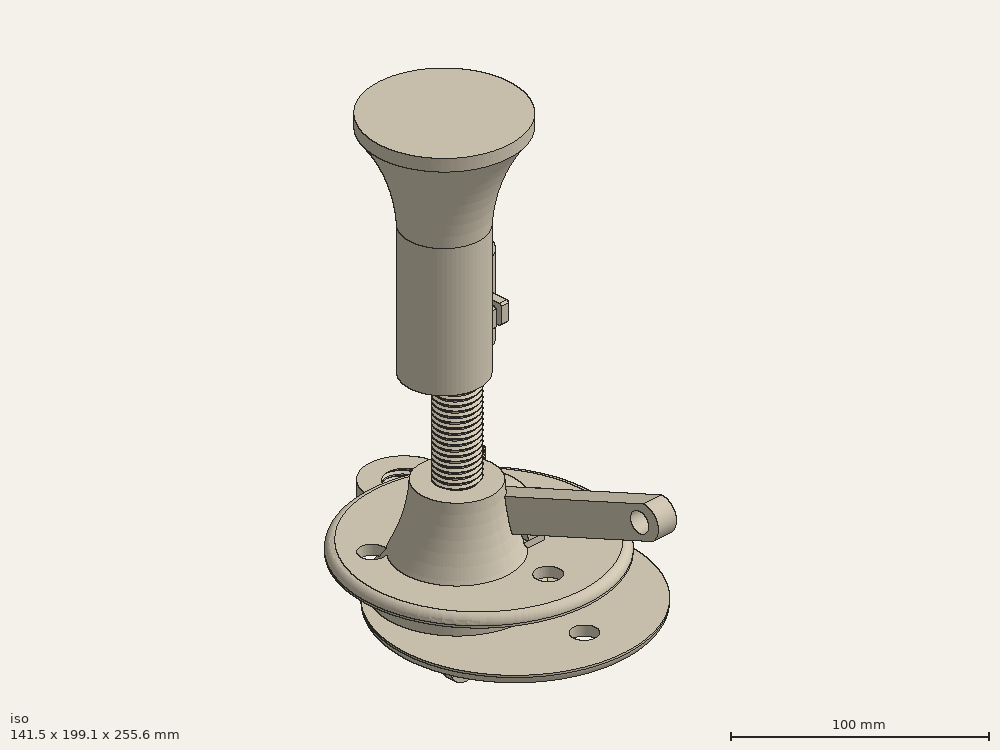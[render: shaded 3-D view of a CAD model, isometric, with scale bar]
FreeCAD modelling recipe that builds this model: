
FCSTD DOCUMENT  (FreeCAD 0.17R13541 (Git))
Label: Projector_stand
License: All rights reserved
LicenseURL: http://en.wikipedia.org/wiki/All_rights_reserved
objects: Sketcher::SketchObject×14, PartDesign::Body×8, Part::Feature×8, PartDesign::Pad×7, Part::Cut×7, Part::MultiFuse×4, Part::Box×4, Part::Cylinder×3, App::Part×3, PartDesign::Pocket×3, PartDesign::Groove×2, Part::Chamfer×2, PartDesign::Fillet×2, PartDesign::FeatureBase×2, Part::Extrusion×1
note: 79 computed .brp shape members not serialized (recipe doc carries the construction recipe); baked Part::Feature solids carry a one-line shape summary decoded from their .brp

FEATURE [Sketcher::SketchObject] Sketch
  MapMode = 5
  Support = -> [XY_Plane001]
  sketch-geometry (1):
    g0: Circle CenterX=0 CenterY=0 CenterZ=0 NormalX=0 NormalY=0 NormalZ=1 AngleXU=0 Radius=35.1414
  constraints (1):
    c: Coincident(g0,g-1)
FEATURE [PartDesign::Pad] Pad
  Length = 50
  Length2 = 100
  Profile = -> Sketch
  Type = 0
FEATURE [Sketcher::SketchObject] Sketch001
  MapMode = 5
  Placement = pos=(0,0,0) rot=(0.57735,0.57735,0.57735;2.0944rad)
  Support = -> [YZ_Plane001]
  sketch-geometry (1):
    g0: Circle CenterX=-96.2321 CenterY=54.218 CenterZ=0 NormalX=0 NormalY=0 NormalZ=1 AngleXU=0 Radius=77.7621
FEATURE [PartDesign::Groove] Groove
  Angle = 360
  Axis = (0,0,1)
  Base = (0,0,0)
  BaseFeature = -> Pad
  Profile = -> Sketch001
  ReferenceAxis = -> Z_Axis001
  Reversed = true
FEATURE [PartDesign::Body] Body
  Group = -> [Sketch,Pad,Sketch001,Groove]
  Origin = -> Origin001
  Tip = -> Groove
FEATURE [Part::Feature] Part__Feature  label="ScrewTap-M20x100_"
  Placement = pos=(0,0,149.5) rot=(0,0,1;0rad)
  shape: bbox 26.45 x 29.66 x 107.5 mm, 170 faces (baked)
FEATURE [Sketcher::SketchObject] Sketch002
  MapMode = 5
  Support = -> [XY_Plane002]
  sketch-geometry (1):
    g0: Circle CenterX=0 CenterY=0 CenterZ=0 NormalX=0 NormalY=0 NormalZ=1 AngleXU=0 Radius=35.1414
  constraints (1):
    c: Coincident(g0,g-1)
FEATURE [PartDesign::Pad] Pad001
  Length = 50
  Length2 = 100
  Profile = -> Sketch002
  Type = 0
FEATURE [Sketcher::SketchObject] Sketch003
  MapMode = 5
  Placement = pos=(0,0,0) rot=(0.57735,0.57735,0.57735;2.0944rad)
  Support = -> [YZ_Plane002]
  sketch-geometry (1):
    g0: Circle CenterX=-96.2321 CenterY=54.218 CenterZ=0 NormalX=0 NormalY=0 NormalZ=1 AngleXU=0 Radius=77.7621
FEATURE [PartDesign::Groove] Groove001
  Angle = 360
  Axis = (0,0,1)
  Base = (0,0,0)
  BaseFeature = -> Pad001
  Profile = -> Sketch003
  ReferenceAxis = -> Z_Axis002
  Reversed = true
FEATURE [PartDesign::Body] Body001
  Group = -> [Sketch002,Pad001,Sketch003,Groove001]
  Origin = -> Origin002
  Placement = pos=(75,0,0) rot=(0,0,1;0rad)
  Tip = -> Groove001
FEATURE [Part::MultiFuse] Fusion  label="Press_fit_bottom"
  Shapes = -> [Body,Part__Feature]
FEATURE [Part::Feature] Part__Feature001  label="ScrewTap-M20x100_001"
  Placement = pos=(75,0,116.5) rot=(0,0,1;0rad)
  shape: bbox 26.45 x 29.66 x 107.5 mm, 170 faces (baked)
FEATURE [Part::Cylinder] Cylinder
  Angle = 360
  AttacherType = Attacher::AttachEngine3D
  Height = 66
  Placement = pos=(75,0,50) rot=(0,0,1;0rad)
  Radius = 18.6
FEATURE [Part::MultiFuse] Fusion001
  Shapes = -> [Cylinder,Body001]
FEATURE [Part::Cut] Cut  label="Press_fit_top"
  Base = -> Fusion001
  Placement = pos=(-82,0,217) rot=(1,0,0;3.14159rad)
  Tool = -> Part__Feature001
FEATURE [Part::Cylinder] Cylinder001
  Angle = 360
  AttacherType = Attacher::AttachEngine3D
  Height = 10
  Placement = pos=(75,80,50) rot=(0,0,1;0rad)
  Radius = 18.5
FEATURE [Part::Feature] Part__Feature002  label="ScrewTap-M20x100_002"
  Placement = pos=(75,80,130.5) rot=(0,0,1;0rad)
  shape: bbox 26.45 x 29.66 x 107.5 mm, 170 faces (baked)
FEATURE [Part::Cut] Cut001
  Base = -> Cylinder001
  Tool = -> Part__Feature002
FEATURE [Part::Feature] Part__Feature003  label="Lock_screw"
  Placement = pos=(66,53,0) rot=(0,1,0;3.14159rad)
  shape: bbox 7.201 x 7 x 20.61 mm, 115 faces (baked)
FEATURE [Part::Box] Box  label="Cube"
  AttacherType = Attacher::AttachEngine3D
  Height = 10
  Length = 13
  Placement = pos=(68.5,52,50) rot=(0,0,1;0rad)
  Width = 14
FEATURE [Part::Feature] Part__Feature004  label="ISO14579-M4x16_001"
  Placement = pos=(82,57,55) rot=(0,1,0;1.5708rad)
  shape: bbox 20.61 x 7 x 7.201 mm, 115 faces (baked)
FEATURE [Part::Box] Box001  label="Cube001"
  AttacherType = Attacher::AttachEngine3D
  Height = 10
  Length = 3
  Placement = pos=(73.5,51,50) rot=(0,0,1;0rad)
  Width = 22
FEATURE [Part::MultiFuse] Fusion002
  Shapes = -> [Box,Cut001]
FEATURE [Part::Cut] Cut002
  Base = -> Fusion002
  Tool = -> Box001
FEATURE [Part::Cut] Cut003
  Base = -> Cut002
  Tool = -> Part__Feature004
FEATURE [Part::Chamfer] Chamfer  label="Lock"
  Base = -> Cut003
  Edges = 9 edges r=1: [Edge1,Edge2,Edge4,Edge12,Edge167,Edge168,Edge169,Edge199,Edge200]
  Placement = pos=(-37,-13,-53) rot=(0,0,1;0rad)
FEATURE [App::Part] Part  label="Projector holder"
  Group = -> [Body,Part__Feature,Fusion,Fusion001,Part__Feature001,Body001,Cylinder,Cut,Part__Feature003,Cut002,Cut003,Fusion002,Cut001,Part__Feature002,Cylinder001,Box,Box001,Part__Feature004,Chamfer]
  License = CC BY 3.0
  LicenseURL = http://creativecommons.org/licenses/by/3.0/
  Origin = -> Origin
  Placement = pos=(0,-127,0) rot=(0,0,1;0rad)
FEATURE [Part::Feature] Part__Feature005  label="ISO14579-M4x16_002"
  Placement = pos=(82,57,71) rot=(0,1,0;1.5708rad)
  shape: bbox 20.61 x 7 x 7.201 mm, 115 faces (baked)
FEATURE [Part::Feature] Part__Feature006  label="Shaft_Lock_Screw"
  Placement = pos=(66,53,0) rot=(0,1,0;3.14159rad)
  shape: bbox 7.201 x 7 x 20.61 mm, 115 faces (baked)
FEATURE [Part::Feature] Part__Feature007  label="ScrewTap-M20x100_003"
  Placement = pos=(75,80,130.5) rot=(0,0,1;0rad)
  shape: bbox 26.45 x 29.66 x 107.5 mm, 170 faces (baked)
FEATURE [Part::Cylinder] Cylinder002
  Angle = 360
  AttacherType = Attacher::AttachEngine3D
  Height = 40
  Placement = pos=(75,80,50) rot=(0,0,1;0rad)
  Radius = 18.5
FEATURE [Part::Cut] Cut006
  Base = -> Cylinder002
  Tool = -> Part__Feature007
FEATURE [Part::Box] Box002  label="Cube002"
  AttacherType = Attacher::AttachEngine3D
  Height = 10
  Length = 13
  Placement = pos=(68.5,52,66) rot=(0,0,1;0rad)
  Width = 14
FEATURE [Part::MultiFuse] Fusion003
  Shapes = -> [Box002,Cut006]
FEATURE [Part::Box] Box003  label="Cube003"
  AttacherType = Attacher::AttachEngine3D
  Height = 42
  Length = 3
  Placement = pos=(73.5,51,50) rot=(0,0,1;0rad)
  Width = 22
FEATURE [Part::Cut] Cut005
  Base = -> Fusion003
  Tool = -> Box003
FEATURE [Part::Cut] Cut004
  Base = -> Cut005
  Tool = -> Part__Feature005
FEATURE [Part::Chamfer] Chamfer001
  Base = -> Cut004
  Edges = 10 edges r=1: [Edge1,Edge2,Edge4,Edge12,Edge13,Edge351,Edge352,Edge353,Edge354,Edge356]
FEATURE [Sketcher::SketchObject] Sketch006
  MapMode = 5
  Placement = pos=(0,0,0) rot=(0.57735,0.57735,0.57735;2.0944rad)
  Support = -> [YZ_Plane005]
  sketch-geometry (4):
    g0: LineSegment StartX=-5.65339 StartY=-7.82598 StartZ=0 EndX=100 EndY=-7.82598 EndZ=0
    g1: LineSegment StartX=100 StartY=7.82598 StartZ=0 EndX=-5.65339 EndY=7.82598 EndZ=0
    g2: ArcOfCircle CenterX=-2.71339 CenterY=0 CenterZ=0 NormalX=0 NormalY=0 NormalZ=1 AngleXU=0 Radius=8.36 StartAngle=1.93016 EndAngle=4.35303
    g3: ArcOfCircle CenterX=97.06 CenterY=0 CenterZ=0 NormalX=0 NormalY=0 NormalZ=1 AngleXU=0 Radius=8.36 StartAngle=5.07175 EndAngle=7.49462
  constraints (12):
    c: Horizontal(g0)
    c: Horizontal(g1)
    c: Equal(g1,g0)
    c: PointOnObject(g2,g-1)
    c: Coincident(g2,g1)
    c: Coincident(g2,g0)
    c: PointOnObject(g3,g-1)
    c: Coincident(g3,g1)
    c: Coincident(g3,g0)
    c: Radius(g2) = 8.36
    c: Equal(g0,g1)
    c: DistanceX(g-1,g0) = 100
FEATURE [PartDesign::Pad] Pad002
  Length = 10
  Length2 = 100
  Placement = pos=(0,0,0) rot=(0.57735,0.57735,0.57735;2.0944rad)
  Profile = -> Sketch006
  Type = 0
FEATURE [Sketcher::SketchObject] Sketch007
  MapMode = 5
  Placement = pos=(0,0,0) rot=(0.57735,0.57735,0.57735;2.0944rad)
  Support = -> [YZ_Plane005]
  sketch-geometry (2):
    g0: Circle CenterX=-1 CenterY=0 CenterZ=0 NormalX=0 NormalY=0 NormalZ=1 AngleXU=0 Radius=5
    g1: Circle CenterX=95 CenterY=0.096219 CenterZ=0 NormalX=0 NormalY=0 NormalZ=1 AngleXU=0 Radius=5
  constraints (5):
    c: PointOnObject(g0,g-1)
    c: DistanceX(g0,g1) = 96
    c: DistanceX(g0,g-1) = 1
    c: Radius(g0) = 5
    c: Radius(g1) = 5
FEATURE [PartDesign::Pocket] Pocket001
  BaseFeature = -> Pad002
  Length = 11
  Length2 = 100
  Placement = pos=(0,0,0) rot=(0.57735,0.57735,0.57735;2.0944rad)
  Profile = -> Sketch007
  Reversed = true
  Type = 0
FEATURE [PartDesign::Body] Body003  label="Arm_shaft"
  Group = -> [Sketch006,Pad002,Sketch007,Pocket001]
  Origin = -> Origin005
  Placement = pos=(10,-1,31) rot=(1,0,0;2.79253rad)
  Tip = -> Pocket001
FEATURE [Sketcher::SketchObject] Sketch008
  MapMode = 5
  Placement = pos=(0,0,0) rot=(0.57735,0.57735,0.57735;2.0944rad)
  Support = -> [YZ_Plane007]
  sketch-geometry (5):
    g0: ArcOfCircle CenterX=0 CenterY=0 CenterZ=0 NormalX=0 NormalY=0 NormalZ=1 AngleXU=0 Radius=18.0424 StartAngle=4.71239 EndAngle=7.85398
    g1: LineSegment StartX=0 StartY=-18.0424 StartZ=0 EndX=-5.9579 EndY=-18.0424 EndZ=0
    g2: LineSegment StartX=-5.9579 StartY=-18.0424 StartZ=0 EndX=-5.9579 EndY=18.0424 EndZ=0
    g3: LineSegment StartX=0 StartY=18.0424 StartZ=0 EndX=-5.9579 EndY=18.0424 EndZ=0
    g4: Circle CenterX=10 CenterY=0 CenterZ=0 NormalX=0 NormalY=0 NormalZ=1 AngleXU=0 Radius=5
  constraints (13):
    c: Coincident(g0,g-1)
    c: PointOnObject(g0,g-2)
    c: PointOnObject(g0,g-2)
    c: Coincident(g1,g0)
    c: Horizontal(g1)
    c: Coincident(g2,g1)
    c: Vertical(g2)
    c: Coincident(g3,g0)
    c: Coincident(g3,g2)
    c: Horizontal(g3)
    c: PointOnObject(g4,g-1)
    c: Radius(g4) = 5
    c: DistanceX(g-1,g4) = 10
FEATURE [PartDesign::Pad] Pad003
  Length = 30
  Length2 = 100
  Placement = pos=(0,0,0) rot=(0.57735,0.57735,0.57735;2.0944rad)
  Profile = -> Sketch008
  Type = 0
FEATURE [Sketcher::SketchObject] Sketch009
  MapMode = 5
  Support = -> [XY_Plane007]
  sketch-geometry (4):
    g0: LineSegment StartX=9 StartY=0 StartZ=0 EndX=21 EndY=0 EndZ=0
    g1: LineSegment StartX=21 StartY=0 StartZ=0 EndX=21 EndY=21.7 EndZ=0
    g2: LineSegment StartX=21 StartY=21.7 StartZ=0 EndX=9 EndY=21.7 EndZ=0
    g3: LineSegment StartX=9 StartY=21.7 StartZ=0 EndX=9 EndY=0 EndZ=0
  constraints (12):
    c: Coincident(g0,g1)
    c: Coincident(g1,g2)
    c: Coincident(g2,g3)
    c: Coincident(g3,g0)
    c: Horizontal(g0)
    c: Horizontal(g2)
    c: Vertical(g1)
    c: Vertical(g3)
    c: PointOnObject(g0,g-1)
    c: DistanceX(g-1,g2) = 9
    c: DistanceY(g0,g1) = 21.7
    c: DistanceX(g2,g1) = 12
FEATURE [PartDesign::Pocket] Pocket002
  BaseFeature = -> Pad003
  Length = 40
  Length2 = 100
  Midplane = true
  Placement = pos=(0,0,0) rot=(0.57735,0.57735,0.57735;2.0944rad)
  Profile = -> Sketch009
  Type = 0
FEATURE [Sketcher::SketchObject] Sketch010
  AttachmentOffset = pos=(12,0,3) rot=(0,0,1;0rad)
  MapMode = 5
  Placement = pos=(12,-3,0) rot=(1,0,0;1.5708rad)
  Support = -> [XZ_Plane007]
  sketch-geometry (4):
    g0: Circle CenterX=0 CenterY=0 CenterZ=0 NormalX=0 NormalY=0 NormalZ=1 AngleXU=0 Radius=60
    g1: Circle CenterX=0.190896 CenterY=37.9247 CenterZ=0 NormalX=0 NormalY=0 NormalZ=1 AngleXU=0 Radius=6
    g2: Circle CenterX=-36 CenterY=-22.55 CenterZ=0 NormalX=0 NormalY=0 NormalZ=1 AngleXU=0 Radius=6
    g3: Circle CenterX=40 CenterY=-8.84 CenterZ=0 NormalX=0 NormalY=0 NormalZ=1 AngleXU=0 Radius=6
  constraints (9):
    c: Coincident(g0,g-1)
    c: Radius(g0) = 60
    c: Radius(g1) = 6
    c: Radius(g2) = 6
    c: Radius(g3) = 6
    c: DistanceX(g2,g-1) = 36
    c: DistanceY(g2,g-1) = 22.55
    c: DistanceX(g-1,g3) = 40
    c: DistanceY(g3,g-1) = 8.84
FEATURE [PartDesign::Pad] Pad004
  BaseFeature = -> Pocket002
  Length = 5
  Length2 = 100
  Placement = pos=(0,0,0) rot=(0.57735,0.57735,0.57735;2.0944rad)
  Profile = -> Sketch010
  Type = 0
FEATURE [Sketcher::SketchObject] Sketch011
  MapMode = 5
  Placement = pos=(0,0,0) rot=(1,0,0;1.5708rad)
  Support = -> [XZ_Plane008]
  sketch-geometry (4):
    g0: Circle CenterX=0 CenterY=0 CenterZ=0 NormalX=0 NormalY=0 NormalZ=1 AngleXU=0 Radius=60
    g1: Circle CenterX=-0.0121047 CenterY=38 CenterZ=0 NormalX=0 NormalY=0 NormalZ=1 AngleXU=0 Radius=6
    g2: Circle CenterX=-36 CenterY=-23 CenterZ=0 NormalX=0 NormalY=0 NormalZ=1 AngleXU=0 Radius=6
    g3: Circle CenterX=40 CenterY=-9 CenterZ=0 NormalX=0 NormalY=0 NormalZ=1 AngleXU=0 Radius=6
  constraints (10):
    c: Coincident(g0,g-1)
    c: Radius(g0) = 60
    c: Radius(g1) = 6
    c: Radius(g2) = 6
    c: Radius(g3) = 6
    c: DistanceX(g2,g-1) = 36
    c: DistanceY(g2,g-1) = 23
    c: DistanceX(g-1,g3) = 40
    c: DistanceY(g3,g-1) = 9
    c: DistanceY(g-1,g1) = 38
FEATURE [PartDesign::Pad] Pad005
  Length = 5
  Length2 = 100
  Placement = pos=(0,0,0) rot=(1,0,0;1.5708rad)
  Profile = -> Sketch011
  Type = 0
FEATURE [PartDesign::Fillet] Fillet001
  Base = -> Pad005 [Edge3]
  BaseFeature = -> Pad005
  Placement = pos=(0,0,0) rot=(1,0,0;1.5708rad)
  Radius = 4
FEATURE [PartDesign::Body] Body005  label="Arms_holder_bottom"
  Group = -> [Sketch011,Pad005,Fillet001]
  Origin = -> Origin008
  Placement = pos=(12,-20,0) rot=(1,0,0;1.5708rad)
  Tip = -> Fillet001
FEATURE [PartDesign::Fillet] Fillet
  Base = -> Pad004 [Edge19]
  BaseFeature = -> Pad004
  Placement = pos=(0,0,0) rot=(0.57735,0.57735,0.57735;2.0944rad)
  Radius = 4
FEATURE [PartDesign::Body] Body004  label="Arms_holder_top"
  Group = -> [Sketch008,Pad003,Sketch009,Pocket002,Sketch010,Pad004,Fillet]
  Origin = -> Origin007
  Placement = pos=(0,0,21) rot=(1,0,0;1.5708rad)
  Tip = -> Fillet
FEATURE [PartDesign::Body] BaseFeatureBody
  Origin = -> Origin009
FEATURE [Sketcher::SketchObject] Sketch012
  MapMode = 5
  Placement = pos=(0,0,0) rot=(1,0,0;1.5708rad)
  Support = -> [XZ_Plane010]
  sketch-geometry (4):
    g0: LineSegment StartX=8.49975 StartY=30.0629 StartZ=0 EndX=8.49975 EndY=-30 EndZ=0
    g1: LineSegment StartX=-8.50025 StartY=-30.0629 StartZ=0 EndX=-8.50025 EndY=30 EndZ=0
    g2: ArcOfCircle CenterX=0 CenterY=-30.0984 CenterZ=0 NormalX=0 NormalY=0 NormalZ=1 AngleXU=0 Radius=8.50032 StartAngle=3.13742 EndAngle=6.29476
    g3: ArcOfCircle CenterX=0 CenterY=29.9645 CenterZ=0 NormalX=0 NormalY=0 NormalZ=1 AngleXU=0 Radius=8.50032 StartAngle=0.0115719 EndAngle=3.13742
  constraints (12):
    c: Vertical(g0)
    c: Vertical(g1)
    c: DistanceY(g-1,g1) = 30
    c: DistanceY(g0,g-1) = 30
    c: Equal(g0,g1)
    c: PointOnObject(g2,g-2)
    c: Coincident(g2,g1)
    c: Coincident(g2,g0)
    c: PointOnObject(g3,g-2)
    c: Coincident(g3,g1)
    c: Coincident(g3,g0)
    c: DistanceX(g1,g0) = 17
FEATURE [PartDesign::Pad] Pad006
  Length = 5
  Length2 = 100
  Placement = pos=(0,0,0) rot=(1,0,0;1.5708rad)
  Profile = -> Sketch012
  Type = 0
FEATURE [Sketcher::SketchObject] Sketch013
  MapMode = 5
  Placement = pos=(0,0,0) rot=(1,0,0;1.5708rad)
  Support = -> [XZ_Plane010]
  sketch-geometry (4):
    g0: LineSegment StartX=3.00034 StartY=29.9949 StartZ=0 EndX=3.00034 EndY=-29.8907 EndZ=0
    g1: LineSegment StartX=-2.99966 StartY=-29.9144 StartZ=0 EndX=-2.99966 EndY=29.9751 EndZ=0
    g2: ArcOfCircle CenterX=0.0013449 CenterY=29.682 CenterZ=0 NormalX=0 NormalY=0 NormalZ=1 AngleXU=0 Radius=3.01528 StartAngle=0.103975 EndAngle=3.04423
    g3: ArcOfCircle CenterX=0 CenterY=-29.8154 CenterZ=0 NormalX=0 NormalY=0 NormalZ=1 AngleXU=0 Radius=3.00129 StartAngle=3.17458 EndAngle=6.25808
  constraints (8):
    c: Vertical(g0)
    c: Vertical(g1)
    c: Coincident(g2,g1)
    c: Coincident(g2,g0)
    c: PointOnObject(g3,g-2)
    c: Coincident(g3,g1)
    c: Coincident(g3,g0)
    c: DistanceX(g1,g0) = 6
FEATURE [PartDesign::Body] Body006  label="Tentacle_1"
  Group = -> [Sketch012,Pad006,Sketch013]
  Origin = -> Origin010
  Tip = -> Pad006
FEATURE [App::Part] Part001  label="Projector_arm"
  Group = -> [Part__Feature006,Part__Feature007,Cut006,Cut005,Cut004,Part__Feature005,Fusion003,Cylinder002,Box002,Box003,Chamfer001,BaseFeature,Body004,Body005,BaseFeatureBody,Body006]
  License = CC BY 3.0
  LicenseURL = http://creativecommons.org/licenses/by/3.0/
  Origin = -> Origin003
FEATURE [Sketcher::SketchObject] Sketch004
  MapMode = 4
  Placement = pos=(0,0,0) rot=(0.57735,0.57735,0.57735;2.0944rad)
  Support = -> [Part001]
  sketch-geometry (3):
    g0: ArcOfCircle CenterX=0 CenterY=0 CenterZ=0 NormalX=0 NormalY=0 NormalZ=1 AngleXU=0 Radius=24.215 StartAngle=4.71239 EndAngle=7.85398
    g1: LineSegment StartX=8e-12 StartY=-24.215 StartZ=0 EndX=1.2e-11 EndY=24.215 EndZ=0
    g2: Circle CenterX=11.89 CenterY=0 CenterZ=0 NormalX=0 NormalY=0 NormalZ=1 AngleXU=0 Radius=6
  constraints (9):
    c: Coincident(g0,g-1)
    c: PointOnObject(g0,g-2)
    c: PointOnObject(g0,g-2)
    c: Coincident(g1,g0)
    c: Coincident(g1,g0)
    c: PointOnObject(g2,g-1)
    c: DistanceY(g0,g0) = 48.43
    c: Radius(g2) = 6
    c: DistanceX(g-1,g2) = 11.89
FEATURE [Part::Extrusion] Extrude
  Base = -> Sketch004
  Dir = (1,0,0)
  DirMode = 2
  FaceMakerClass = Part::FaceMakerBullseye
  LengthFwd = 30
  LengthRev = 0
  Solid = true
  Symmetric = false
FEATURE [Sketcher::SketchObject] Sketch005
  AttachmentOffset = pos=(0,0,-24) rot=(0,0,1;0rad)
  MapMode = 2
  Placement = pos=(0,0,-24) rot=(0,0,1;0rad)
  Support = -> [Extrude]
  sketch-geometry (4):
    g0: LineSegment StartX=8 StartY=27 StartZ=0 EndX=22 EndY=27 EndZ=0
    g1: LineSegment StartX=22 StartY=27 StartZ=0 EndX=22 EndY=-1 EndZ=0
    g2: LineSegment StartX=22 StartY=-1 StartZ=0 EndX=8 EndY=-1 EndZ=0
    g3: LineSegment StartX=8 StartY=-1 StartZ=0 EndX=8 EndY=27 EndZ=0
  constraints (12):
    c: Coincident(g0,g1)
    c: Coincident(g1,g2)
    c: Coincident(g2,g3)
    c: Coincident(g3,g0)
    c: Horizontal(g0)
    c: Horizontal(g2)
    c: Vertical(g1)
    c: Vertical(g3)
    c: DistanceY(g2,g0) = 28
    c: DistanceX(g2,g1) = 14
    c: DistanceX(g-1,g1) = 22
    c: DistanceY(g-1,g0) = 27
FEATURE [PartDesign::Body] Body002
  BaseFeature = -> Pocket
  Group = -> [BaseFeature001]
  Origin = -> Origin004
  Tip = -> BaseFeature001
FEATURE [PartDesign::FeatureBase] BaseFeature
  BaseFeature = -> Extrude
FEATURE [PartDesign::Pocket] Pocket
  Length = 48
  Length2 = 100
  Profile = -> Sketch005
  Reversed = true
  Type = 0
FEATURE [PartDesign::FeatureBase] BaseFeature001
  BaseFeature = -> Pocket
FEATURE [App::Part] Part002
  Group = -> [Body002]
  License = CC BY 3.0
  LicenseURL = http://creativecommons.org/licenses/by/3.0/
  Origin = -> Origin006
